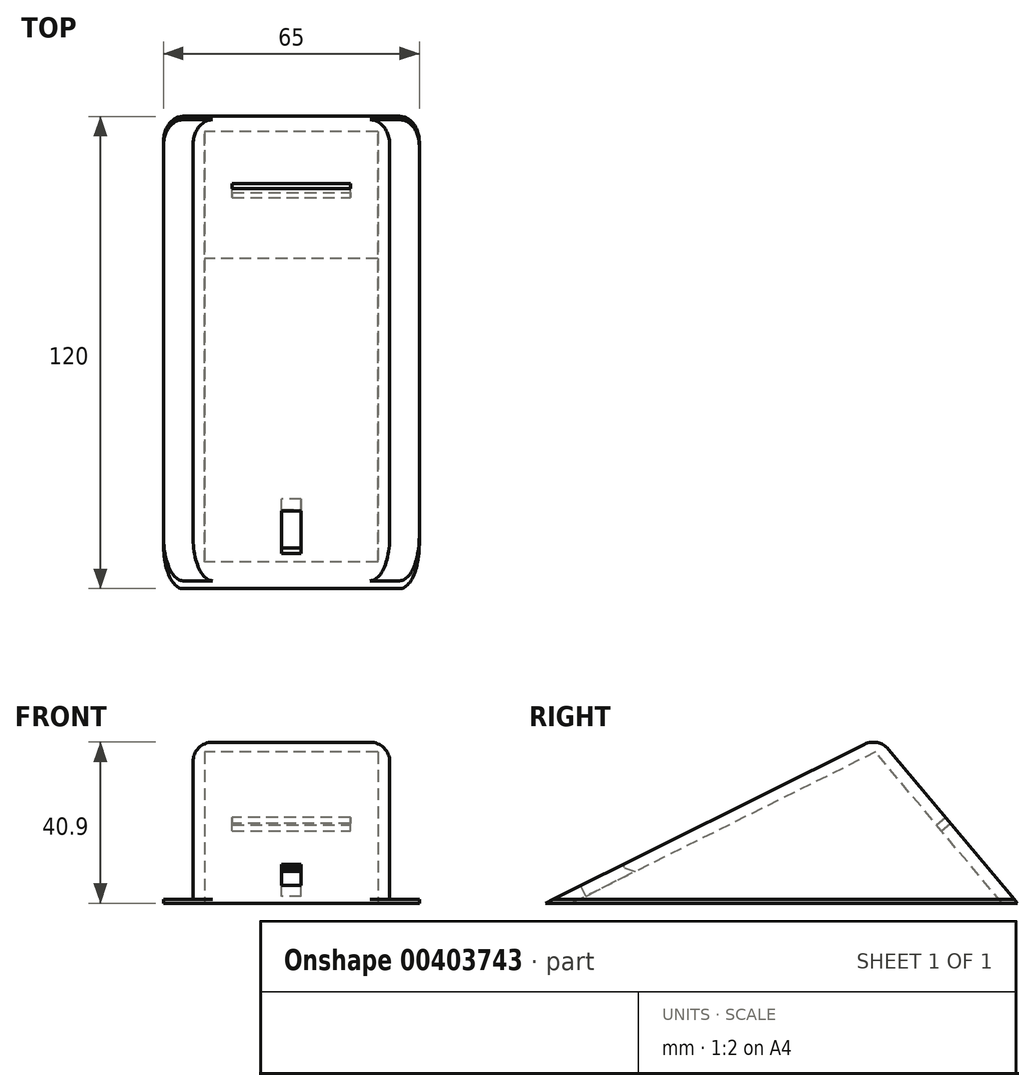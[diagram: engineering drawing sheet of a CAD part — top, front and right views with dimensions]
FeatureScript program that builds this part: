
annotation { "Feature Type Name" : "Feature", "Feature Type Description" : "" }
export const myFeature = defineFeature(function(context is Context, id is Id, definition is map)
    precondition{}
    {
        {
            var Q0;
            Q0=qCreatedBy(makeId("Right.planeOp"),FACE);
            var sketch = newSketch(context, id + "F0", { "sketchPlane" : qUnion([Q0])});
            skLineSegment(sketch, "E0", {"start": v(-56.25, -38.26) * mm, "end": v(63.75, -38.26) * mm});
            skLineSegment(sketch, "E1", {"start": v(63.75, -38.26) * mm, "end": v(28.4, 3.87) * mm});
            skLineSegment(sketch, "E2", {"start": v(28.4, 3.87) * mm, "end": v(-56.25, -38.26) * mm});
            skLineSegment(sketch, "E3", {"start": v(59.84, -38.26) * mm, "end": v(27.62, 0.13) * mm});
            skLineSegment(sketch, "E4", {"start": v(27.62, 0.13) * mm, "end": v(-49.51, -38.26) * mm});
            skSolve(sketch);
        }
        {
            var Q0;
            {var subQ1=sQuery(id+"F0.wireOp",EDGE,"E1");Q0=makeQuery(id+"F0.imprint","IMPRINT",FACE,{"disambiguationData":[TD([[makeQuery(id+"F0.imprint","IMPRINT",EDGE,{"derivedFrom":subQ1}),1.0]])]});}
            extrude(context, id + "F1", {"entities" : qUnion([Q0]), "depth" : 50 * mm});
        }
        {
            var Q0;
            {var subQ0=sQuery(id+"F0.wireOp",EDGE,"E3");Q0=makeQuery(id+"F0.imprint","IMPRINT",FACE,{"disambiguationData":[TD([[makeQuery(id+"F0.imprint","IMPRINT",EDGE,{"derivedFrom":subQ0}),1.0]])]});}
            extrude(context, id + "F2", {"entities" : qUnion([Q0]), "operationType" : NewBodyOperationType.ADD, "depth" : 3 * mm});
        }
        {
            var Q0;
            Q0=makeQuery(id+"F1.opExtrude","CAP_FACE",FACE,{"disambiguationData":[OSD([sQuery(id+"F0.wireOp",EDGE,"E0"),sQuery(id+"F0.wireOp",EDGE,"E1"),sQuery(id+"F0.wireOp",EDGE,"E2"),sQuery(id+"F0.wireOp",EDGE,"E3"),sQuery(id+"F0.wireOp",EDGE,"E4")])],"isStart":false});
            var sketch = newSketch(context, id + "F3", { "sketchPlane" : qUnion([Q0])});
            skLineSegment(sketch, "E5", {"start": v(-49.51, -38.26) * mm, "end": v(59.84, -38.26) * mm});
            skLineSegment(sketch, "E6", {"start": v(59.84, -38.26) * mm, "end": v(27.62, 0.13) * mm});
            skLineSegment(sketch, "E7", {"start": v(27.62, 0.13) * mm, "end": v(-49.51, -38.26) * mm});
            skSolve(sketch);
        }
        {
            var Q0;
            Q0=makeQuery(id+"F3.imprint","IMPRINT",FACE,{"disambiguationData":[TD([[makeQuery(id+"F3.imprint","IMPRINT",EDGE,{"derivedFrom":sQuery(id+"F3.wireOp",EDGE,"E5")}),1.0]])]});
            extrude(context, id + "F4", {"entities" : qUnion([Q0]), "operationType" : NewBodyOperationType.ADD, "oppositeDirection" : true, "depth" : 3 * mm});
        }
        {
            var Q0;
            Q0=makeQuery(id+"F1.opExtrude","SWEPT_FACE",FACE,{"disambiguationData":[OSD([sQuery(id+"F0.wireOp",EDGE,"E1")])]});
            var sketch = newSketch(context, id + "F5", { "sketchPlane" : qUnion([Q0])});
            skLineSegment(sketch, "E8", {"start": v(-50, -43.8) * mm, "end": v(0, -43.8) * mm});
            skLineSegment(sketch, "E9", {"start": v(-50, -41.8) * mm, "end": v(0, -41.8) * mm});
            skLineSegment(sketch, "E10", {"start": v(-50, -15.3) * mm, "end": v(-50, -70.3) * mm});
            skLineSegment(sketch, "E11", {"start": v(-50, -70.3) * mm, "end": v(0, -70.3) * mm});
            skLineSegment(sketch, "E12", {"start": v(-10, -41.8) * mm, "end": v(-10, -43.8) * mm});
            skLineSegment(sketch, "E13", {"start": v(-40, -41.8) * mm, "end": v(-40, -43.8) * mm});
            skSolve(sketch);
        }
        {
            var Q0;
            {var subQ0=sQuery(id+"F5.wireOp",EDGE,"E12");Q0=makeQuery(id+"F5.imprint","IMPRINT",FACE,{"disambiguationData":[TD([[makeQuery(id+"F5.imprint","IMPRINT",EDGE,{"derivedFrom":subQ0}),-1.0]])]});}
            extrude(context, id + "F6", {"entities" : qUnion([Q0]), "operationType" : NewBodyOperationType.REMOVE, "oppositeDirection" : true, "depth" : 25 * mm});
        }
        {
            var Q0;
            Q0=makeQuery(id+"F1.opExtrude","SWEPT_FACE",FACE,{"disambiguationData":[OSD([sQuery(id+"F0.wireOp",EDGE,"E2")])]});
            var sketch = newSketch(context, id + "F7", { "sketchPlane" : qUnion([Q0])});
            skLineSegment(sketch, "E14", {"start": v(0, -57.4) * mm, "end": v(50, -57.4) * mm});
            skLineSegment(sketch, "E15", {"start": v(0, -45.4) * mm, "end": v(50, -45.4) * mm});
            skLineSegment(sketch, "E16", {"start": v(22.5, -45.4) * mm, "end": v(22.5, -57.4) * mm});
            skLineSegment(sketch, "E17", {"start": v(27.5, -45.4) * mm, "end": v(27.5, -57.4) * mm});
            skSolve(sketch);
        }
        {
            var Q0;
            {var subQ0=sQuery(id+"F7.wireOp",EDGE,"E16");Q0=makeQuery(id+"F7.imprint","IMPRINT",FACE,{"disambiguationData":[TD([[makeQuery(id+"F7.imprint","IMPRINT",EDGE,{"derivedFrom":subQ0}),1.0]])]});}
            extrude(context, id + "F8", {"entities" : qUnion([Q0]), "operationType" : NewBodyOperationType.REMOVE, "oppositeDirection" : true, "depth" : 25 * mm});
        }
        {
            var Q0;
            Q0=makeQuery(id+"F8.boolean.opBoolean","INTERSECT",EDGE,{"derivedFrom":[makeQuery(id+"F1.opExtrude","SWEPT_FACE",FACE,{"disambiguationData":[OSD([sQuery(id+"F0.wireOp",EDGE,"E4")])]}),makeQuery(id+"F8.opExtrude","SWEPT_FACE",FACE,{"disambiguationData":[OSD([sQuery(id+"F7.wireOp",EDGE,"E15")])]})]});
            chamfer(context, id + "F9", {"entities" : qUnion([Q0]), "width" : 2 * mm, "tangentPropagation" : true});
        }
        {
            var Q0;
            {var subQ0=sQuery(id+"F0.wireOp",EDGE,"E4");var subQ1=sQuery(id+"F0.wireOp",EDGE,"E3");var subQ2=sQuery(id+"F0.wireOp",EDGE,"E0");Q0=makeQuery(id+"F2.boolean.opBoolean","MERGE",FACE,{"derivedFrom":[makeQuery(id+"F1.opExtrude","CAP_FACE",FACE,{"disambiguationData":[OSD([subQ2,sQuery(id+"F0.wireOp",EDGE,"E1"),sQuery(id+"F0.wireOp",EDGE,"E2"),subQ1,subQ0])],"isStart":true}),makeQuery(id+"F2.opExtrude","CAP_FACE",FACE,{"disambiguationData":[OSD([subQ2,subQ1,subQ0])],"isStart":true})]});}
            var sketch = newSketch(context, id + "F10", { "sketchPlane" : qUnion([Q0])});
            skLineSegment(sketch, "E18", {"start": v(54.24, -37.26) * mm, "end": v(-62.92, -37.26) * mm});
            skSolve(sketch);
        }
        {
            var Q0;
            {var subQ0=sQuery(id+"F10.wireOp",EDGE,"E18");Q0=makeQuery(id+"F10.imprint","IMPRINT",FACE,{"disambiguationData":[TD([[makeQuery(id+"F10.imprint","IMPRINT",EDGE,{"derivedFrom":subQ0}),1.0]])]});}
            extrude(context, id + "F11", {"entities" : qUnion([Q0]), "operationType" : NewBodyOperationType.ADD, "depth" : 7.5 * mm});
        }
        {
            var Q0;
            Q0=makeQuery(id+"F11.opExtrude","CAP_EDGE",EDGE,{"disambiguationData":[OSD([sQuery(id+"F0.wireOp",EDGE,"E1")])],"isStart":false});
            fillet(context, id + "F12", {"entities" : qUnion([Q0]), "radius" : 5 * mm, "tangentPropagation" : true, "allowEdgeOverflow" : false});
        }
        {
            var Q0;
            Q0=makeQuery(id+"F11.opExtrude","CAP_EDGE",EDGE,{"disambiguationData":[OSD([sQuery(id+"F0.wireOp",EDGE,"E2")])],"isStart":false});
            fillet(context, id + "F13", {"entities" : qUnion([Q0]), "radius" : 5 * mm, "tangentPropagation" : true, "allowEdgeOverflow" : false});
        }
        {
            var Q0;
            Q0=makeQuery(id+"F4.boolean.opBoolean","MERGE",FACE,{"derivedFrom":[makeQuery(id+"F1.opExtrude","CAP_FACE",FACE,{"disambiguationData":[OSD([sQuery(id+"F0.wireOp",EDGE,"E0"),sQuery(id+"F0.wireOp",EDGE,"E1"),sQuery(id+"F0.wireOp",EDGE,"E2"),sQuery(id+"F0.wireOp",EDGE,"E3"),sQuery(id+"F0.wireOp",EDGE,"E4")])],"isStart":false}),makeQuery(id+"F4.opExtrude","CAP_FACE",FACE,{"disambiguationData":[OSD([sQuery(id+"F3.wireOp",EDGE,"E5"),sQuery(id+"F3.wireOp",EDGE,"E6"),sQuery(id+"F3.wireOp",EDGE,"E7")])],"isStart":true})]});
            var sketch = newSketch(context, id + "F14", { "sketchPlane" : qUnion([Q0])});
            skLineSegment(sketch, "E19", {"start": v(62.92, -37.26) * mm, "end": v(-54.24, -37.26) * mm});
            skSolve(sketch);
        }
        {
            var Q0;
            {var subQ0=sQuery(id+"F14.wireOp",EDGE,"E19");Q0=makeQuery(id+"F14.imprint","IMPRINT",FACE,{"disambiguationData":[TD([[makeQuery(id+"F14.imprint","IMPRINT",EDGE,{"derivedFrom":subQ0}),1.0]])]});}
            extrude(context, id + "F15", {"entities" : qUnion([Q0]), "operationType" : NewBodyOperationType.ADD, "depth" : 7.5 * mm});
        }
        {
            var Q0;
            Q0=makeQuery(id+"F15.opExtrude","CAP_EDGE",EDGE,{"disambiguationData":[OSD([sQuery(id+"F0.wireOp",EDGE,"E1")])],"isStart":false});
            fillet(context, id + "F16", {"entities" : qUnion([Q0]), "radius" : 5 * mm, "tangentPropagation" : true, "allowEdgeOverflow" : false});
        }
        {
            var Q0;
            Q0=makeQuery(id+"F15.opExtrude","CAP_EDGE",EDGE,{"disambiguationData":[OSD([sQuery(id+"F0.wireOp",EDGE,"E2")])],"isStart":false});
            fillet(context, id + "F17", {"entities" : qUnion([Q0]), "radius" : 5 * mm, "tangentPropagation" : true, "allowEdgeOverflow" : false});
        }
        {
            var Q0;
            Q0=makeQuery(id+"F1.opExtrude","SWEPT_EDGE",EDGE,{"disambiguationData":[OSD([sQuery(id+"F0.wireOp",EDGE,"E1"),sQuery(id+"F0.wireOp",EDGE,"E2")])]});
            fillet(context, id + "F18", {"entities" : qUnion([Q0]), "radius" : 5 * mm, "tangentPropagation" : true, "allowEdgeOverflow" : false});
        }
        {
            var Q0;
            Q0=makeQuery(id+"F1.opExtrude","CAP_EDGE",EDGE,{"disambiguationData":[OSD([sQuery(id+"F0.wireOp",EDGE,"E2")])],"isStart":false});
            var Q1;
            {var subQ0=sQuery(id+"F0.wireOp",EDGE,"E2");var subQ1=sQuery(id+"F0.wireOp",EDGE,"E1");Q1=makeQuery(id+"F18.opFillet","BLEND_EDGE",EDGE,{"blendedFrom":[makeQuery(id+"F1.opExtrude","SWEPT_EDGE",EDGE,{"disambiguationData":[OSD([subQ1,subQ0])]}),makeQuery(id+"F4.boolean.opBoolean","MERGE",FACE,{"derivedFrom":[makeQuery(id+"F1.opExtrude","CAP_FACE",FACE,{"disambiguationData":[OSD([sQuery(id+"F0.wireOp",EDGE,"E0"),subQ1,subQ0,sQuery(id+"F0.wireOp",EDGE,"E3"),sQuery(id+"F0.wireOp",EDGE,"E4")])],"isStart":false}),makeQuery(id+"F4.opExtrude","CAP_FACE",FACE,{"disambiguationData":[OSD([sQuery(id+"F3.wireOp",EDGE,"E5"),sQuery(id+"F3.wireOp",EDGE,"E6"),sQuery(id+"F3.wireOp",EDGE,"E7")])],"isStart":true})]})],"blendedInto":[makeQuery(id+"F4.boolean.opBoolean","MERGE",FACE,{"derivedFrom":[makeQuery(id+"F1.opExtrude","CAP_FACE",FACE,{"disambiguationData":[OSD([sQuery(id+"F0.wireOp",EDGE,"E0"),subQ1,subQ0,sQuery(id+"F0.wireOp",EDGE,"E3"),sQuery(id+"F0.wireOp",EDGE,"E4")])],"isStart":false}),makeQuery(id+"F4.opExtrude","CAP_FACE",FACE,{"disambiguationData":[OSD([sQuery(id+"F3.wireOp",EDGE,"E5"),sQuery(id+"F3.wireOp",EDGE,"E6"),sQuery(id+"F3.wireOp",EDGE,"E7")])],"isStart":true})]})]});}
            var Q2;
            Q2=makeQuery(id+"F1.opExtrude","CAP_EDGE",EDGE,{"disambiguationData":[OSD([sQuery(id+"F0.wireOp",EDGE,"E1")])],"isStart":false});
            fillet(context, id + "F19", {"entities" : qUnion([Q0, Q1, Q2]), "radius" : 5 * mm, "tangentPropagation" : true, "allowEdgeOverflow" : false});
        }
        {
            var Q0;
            Q0=makeQuery(id+"F1.opExtrude","CAP_EDGE",EDGE,{"disambiguationData":[OSD([sQuery(id+"F0.wireOp",EDGE,"E2")])],"isStart":true});
            fillet(context, id + "F20", {"entities" : qUnion([Q0]), "radius" : 5 * mm, "tangentPropagation" : true, "allowEdgeOverflow" : false});
        }
    });
